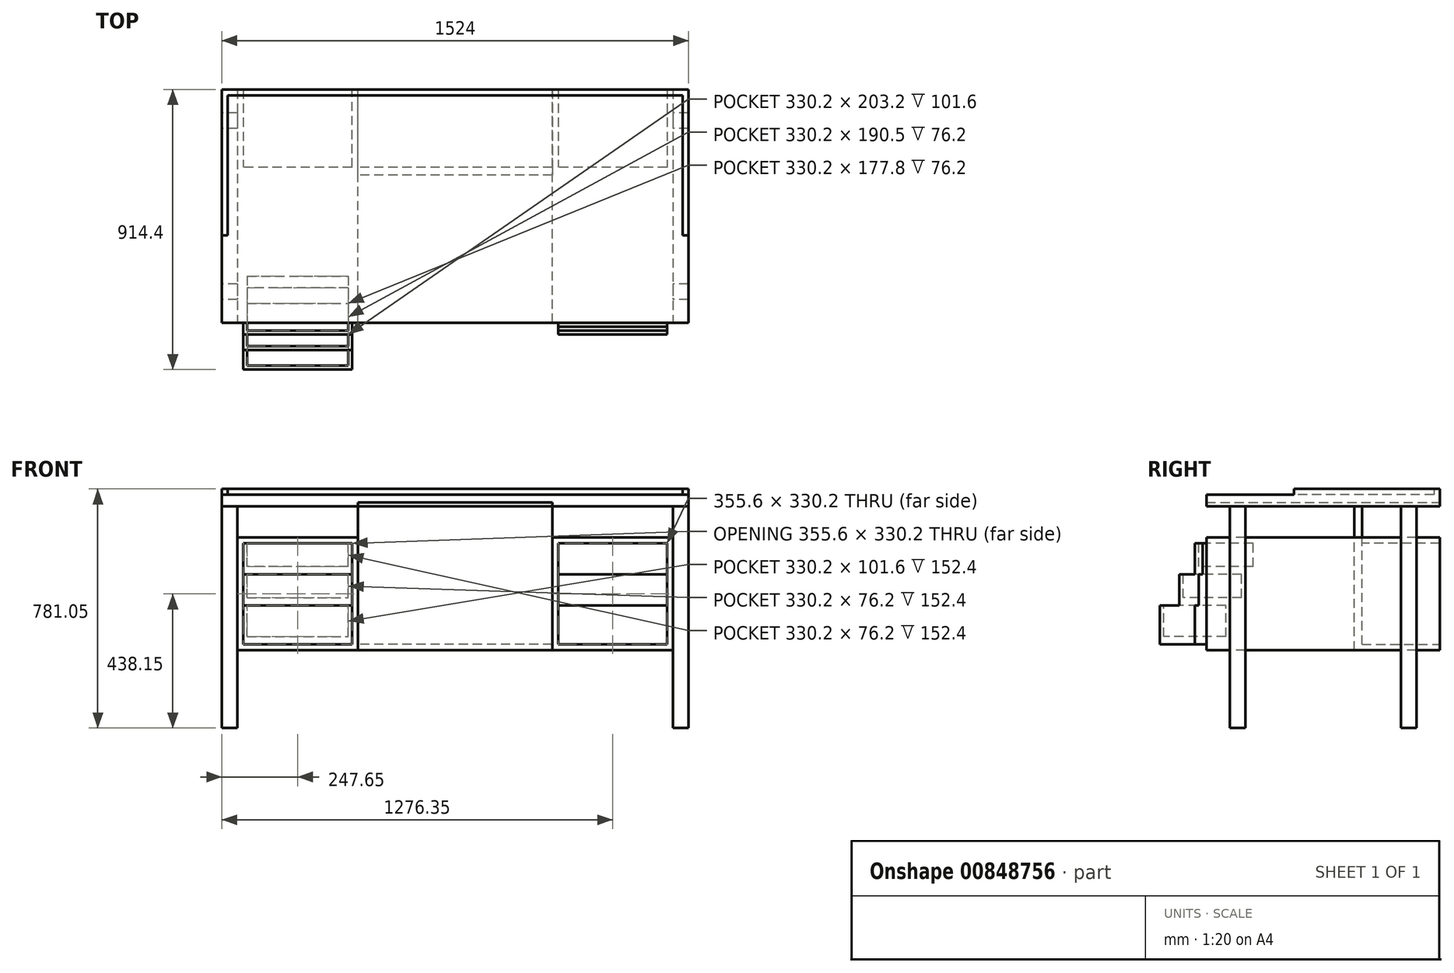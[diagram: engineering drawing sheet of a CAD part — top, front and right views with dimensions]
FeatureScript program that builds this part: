
annotation { "Feature Type Name" : "Feature", "Feature Type Description" : "" }
export const myFeature = defineFeature(function(context is Context, id is Id, definition is map)
    precondition{}
    {
        {
            var Q0;
            Q0=qCreatedBy(makeId("Top.planeOp"),FACE);
            var sketch = newSketch(context, id + "F0", { "sketchPlane" : qUnion([Q0])});
            skLineSegment(sketch, "E0.bottom", {"start": v(-762, -381) * mm, "end": v(762, -381) * mm});
            skLineSegment(sketch, "E0.top", {"start": v(-762, 381) * mm, "end": v(762, 381) * mm});
            skLineSegment(sketch, "E0.left", {"start": v(-762, -381) * mm, "end": v(-762, 381) * mm});
            skLineSegment(sketch, "E0.right", {"start": v(762, -381) * mm, "end": v(762, 381) * mm});
            skPoint(sketch, "E0.middle", {"position": v(0, 0) * mm});
            skSolve(sketch);
        }
        {
            var Q0;
            Q0=makeQuery(id+"F0.imprint","IMPRINT",FACE,{"disambiguationData":[TD([[makeQuery(id+"F0.imprint","IMPRINT",EDGE,{"derivedFrom":sQuery(id+"F0.wireOp",EDGE,"E0.bottom")}),1.0]])]});
            var Q1;
            Q1=sQuery(id+"F0.wireOp",EDGE,"E0.bottom");
            extrude(context, id + "F1", {"entities" : qUnion([Q0]), "surfaceEntities" : qUnion([Q1]), "depth" : 762 * mm, "offsetDistance" : 25.4 * mm});
        }
        {
            var Q0;
            Q0=makeQuery(id+"F1.opExtrude","SWEPT_FACE",FACE,{"disambiguationData":[OSD([sQuery(id+"F0.wireOp",EDGE,"E0.bottom")])]});
            var sketch = newSketch(context, id + "F2", { "sketchPlane" : qUnion([Q0])});
            skLineSegment(sketch, "E1.bottom", {"start": v(-762, 723.9) * mm, "end": v(762, 723.9) * mm});
            skLineSegment(sketch, "E1.top", {"start": v(-762, 622.3) * mm, "end": v(762, 622.3) * mm});
            skLineSegment(sketch, "E1.left", {"start": v(-762, 723.9) * mm, "end": v(-762, 622.3) * mm});
            skLineSegment(sketch, "E1.right", {"start": v(762, 723.9) * mm, "end": v(762, 622.3) * mm});
            skSolve(sketch);
        }
        {
            var Q0;
            Q0=makeQuery(id+"F2.imprint","IMPRINT",FACE,{"disambiguationData":[TD([[makeQuery(id+"F2.imprint","IMPRINT",EDGE,{"derivedFrom":sQuery(id+"F2.wireOp",EDGE,"E1.bottom")}),-1.0]])]});
            var Q1;
            Q1=sQuery(id+"F2.wireOp",EDGE,"E1.right");
            var Q2;
            Q2=sQuery(id+"F2.wireOp",EDGE,"E1.top");
            var Q3;
            Q3=sQuery(id+"F2.wireOp",EDGE,"E1.left");
            var Q4;
            Q4=sQuery(id+"F2.wireOp",EDGE,"E1.bottom");
            extrude(context, id + "F3", {"entities" : qUnion([Q0]), "operationType" : NewBodyOperationType.REMOVE, "surfaceEntities" : qUnion([Q1, Q2, Q3, Q4]), "oppositeDirection" : true, "depth" : 914.4 * mm, "offsetDistance" : 25.4 * mm});
        }
        {
            var Q0;
            Q0=makeQuery(id+"F1.opExtrude","CAP_FACE",FACE,{"disambiguationData":[OSD([sQuery(id+"F0.wireOp",EDGE,"E0.bottom"),sQuery(id+"F0.wireOp",EDGE,"E0.top"),sQuery(id+"F0.wireOp",EDGE,"E0.left"),sQuery(id+"F0.wireOp",EDGE,"E0.right")])],"isStart":true});
            var sketch = newSketch(context, id + "F4", { "sketchPlane" : qUnion([Q0])});
            skLineSegment(sketch, "E2.bottom", {"start": v(0, 0) * mm, "end": v(0, 0) * mm});
            skLineSegment(sketch, "E2.top", {"start": v(0, 0) * mm, "end": v(0, 0) * mm});
            skLineSegment(sketch, "E2.left", {"start": v(0, 0) * mm, "end": v(0, 0) * mm});
            skLineSegment(sketch, "E2.right", {"start": v(0, 0) * mm, "end": v(0, 0) * mm});
            skPoint(sketch, "E2.middle", {"position": v(0, 0) * mm});
            skLineSegment(sketch, "E3.bottom", {"start": v(317.5, 381) * mm, "end": v(-317.5, 381) * mm});
            skLineSegment(sketch, "E3.top", {"start": v(317.5, -381) * mm, "end": v(-317.5, -381) * mm});
            skLineSegment(sketch, "E3.left", {"start": v(317.5, 381) * mm, "end": v(317.5, -381) * mm});
            skLineSegment(sketch, "E3.right", {"start": v(-317.5, 381) * mm, "end": v(-317.5, -381) * mm});
            skSolve(sketch);
        }
        {
            var Q0;
            Q0=qSketchRegion(id+"F4",true);
            extrude(context, id + "F5", {"entities" : qUnion([Q0]), "operationType" : NewBodyOperationType.REMOVE, "oppositeDirection" : true, "depth" : 736.6 * mm, "offsetDistance" : 25.4 * mm});
        }
        {
            var Q0;
            {var subQ0=sQuery(id+"F0.wireOp",EDGE,"E0.bottom");var subQ1=sQuery(id+"F0.wireOp",EDGE,"E0.right");var subQ2=sQuery(id+"F0.wireOp",EDGE,"E0.top");Q0=makeQuery(id+"F5.boolean.opBoolean","SPLIT",FACE,{"disambiguationData":[TD([makeQuery(id+"F1.opExtrude","SWEPT_FACE",FACE,{"disambiguationData":[OSD([subQ1])]})])],"derivedFrom":makeQuery(id+"F1.opExtrude","CAP_FACE",FACE,{"disambiguationData":[OSD([subQ0,subQ2,sQuery(id+"F0.wireOp",EDGE,"E0.left"),subQ1])],"isStart":true})});}
            var sketch = newSketch(context, id + "F6", { "sketchPlane" : qUnion([Q0])});
            skLineSegment(sketch, "E4.bottom", {"start": v(711.2, -381) * mm, "end": v(762, -381) * mm});
            skLineSegment(sketch, "E4.top", {"start": v(711.2, 381) * mm, "end": v(762, 381) * mm});
            skLineSegment(sketch, "E4.left", {"start": v(711.2, -381) * mm, "end": v(711.2, 381) * mm});
            skLineSegment(sketch, "E4.right", {"start": v(762, -381) * mm, "end": v(762, 381) * mm});
            skSolve(sketch);
        }
        {
            var Q0;
            Q0=qSketchRegion(id+"F6",true);
            extrude(context, id + "F7", {"entities" : qUnion([Q0]), "operationType" : NewBodyOperationType.REMOVE, "oppositeDirection" : true, "depth" : 711.2 * mm, "offsetDistance" : 25.4 * mm});
        }
        {
            var Q0;
            {var subQ0=sQuery(id+"F0.wireOp",EDGE,"E0.bottom");var subQ1=sQuery(id+"F0.wireOp",EDGE,"E0.top");var subQ2=sQuery(id+"F0.wireOp",EDGE,"E0.left");Q0=makeQuery(id+"F5.boolean.opBoolean","SPLIT",FACE,{"disambiguationData":[TD([makeQuery(id+"F1.opExtrude","SWEPT_FACE",FACE,{"disambiguationData":[OSD([subQ2])]})])],"derivedFrom":makeQuery(id+"F1.opExtrude","CAP_FACE",FACE,{"disambiguationData":[OSD([subQ0,subQ1,subQ2,sQuery(id+"F0.wireOp",EDGE,"E0.right")])],"isStart":true})});}
            var sketch = newSketch(context, id + "F8", { "sketchPlane" : qUnion([Q0])});
            skLineSegment(sketch, "E5.bottom", {"start": v(-711.2, -381) * mm, "end": v(-762, -381) * mm});
            skLineSegment(sketch, "E5.top", {"start": v(-711.2, 381) * mm, "end": v(-762, 381) * mm});
            skLineSegment(sketch, "E5.left", {"start": v(-711.2, -381) * mm, "end": v(-711.2, 381) * mm});
            skLineSegment(sketch, "E5.right", {"start": v(-762, -381) * mm, "end": v(-762, 381) * mm});
            skSolve(sketch);
        }
        {
            var Q0;
            Q0=qSketchRegion(id+"F8",true);
            extrude(context, id + "F9", {"entities" : qUnion([Q0]), "operationType" : NewBodyOperationType.REMOVE, "oppositeDirection" : true, "depth" : 711.2 * mm, "offsetDistance" : 25.4 * mm});
        }
        {
            var Q0;
            Q0=makeQuery(id+"F3.boolean.opBoolean","COPY",FACE,{"derivedFrom":makeQuery(id+"F3.opExtrude","SWEPT_FACE",FACE,{"disambiguationData":[OSD([sQuery(id+"F2.wireOp",EDGE,"E1.bottom")])]})});
            var sketch = newSketch(context, id + "F10", { "sketchPlane" : qUnion([Q0])});
            skLineSegment(sketch, "E6.bottom", {"start": v(762, 254) * mm, "end": v(711.2, 254) * mm});
            skLineSegment(sketch, "E6.top", {"start": v(762, 304.8) * mm, "end": v(711.2, 304.8) * mm});
            skLineSegment(sketch, "E6.left", {"start": v(762, 254) * mm, "end": v(762, 304.8) * mm});
            skLineSegment(sketch, "E6.right", {"start": v(711.2, 254) * mm, "end": v(711.2, 304.8) * mm});
            skSolve(sketch);
        }
        {
            var Q0;
            Q0=qSketchRegion(id+"F10",true);
            extrude(context, id + "F11", {"entities" : qUnion([Q0]), "depth" : 723.9 * mm, "offsetDistance" : 25.4 * mm});
        }
        {
            var Q0;
            Q0=makeQuery(id+"F3.boolean.opBoolean","COPY",FACE,{"derivedFrom":makeQuery(id+"F3.opExtrude","SWEPT_FACE",FACE,{"disambiguationData":[OSD([sQuery(id+"F2.wireOp",EDGE,"E1.bottom")])]})});
            var sketch = newSketch(context, id + "F12", { "sketchPlane" : qUnion([Q0])});
            skLineSegment(sketch, "E7.bottom", {"start": v(762, -304.8) * mm, "end": v(711.2, -304.8) * mm});
            skLineSegment(sketch, "E7.top", {"start": v(762, -254) * mm, "end": v(711.2, -254) * mm});
            skLineSegment(sketch, "E7.left", {"start": v(762, -304.8) * mm, "end": v(762, -254) * mm});
            skLineSegment(sketch, "E7.right", {"start": v(711.2, -304.8) * mm, "end": v(711.2, -254) * mm});
            skSolve(sketch);
        }
        {
            var Q0;
            Q0=qSketchRegion(id+"F12",true);
            extrude(context, id + "F13", {"entities" : qUnion([Q0]), "depth" : 723.9 * mm, "offsetDistance" : 25.4 * mm});
        }
        {
            var Q0;
            Q0=makeQuery(id+"F3.boolean.opBoolean","COPY",FACE,{"derivedFrom":makeQuery(id+"F3.opExtrude","SWEPT_FACE",FACE,{"disambiguationData":[OSD([sQuery(id+"F2.wireOp",EDGE,"E1.bottom")])]})});
            var sketch = newSketch(context, id + "F14", { "sketchPlane" : qUnion([Q0])});
            skLineSegment(sketch, "E8.bottom", {"start": v(-711.2, 254) * mm, "end": v(-762, 254) * mm});
            skLineSegment(sketch, "E8.top", {"start": v(-711.2, 304.8) * mm, "end": v(-762, 304.8) * mm});
            skLineSegment(sketch, "E8.left", {"start": v(-711.2, 254) * mm, "end": v(-711.2, 304.8) * mm});
            skLineSegment(sketch, "E8.right", {"start": v(-762, 254) * mm, "end": v(-762, 304.8) * mm});
            skSolve(sketch);
        }
        {
            var Q0;
            Q0=qSketchRegion(id+"F14",true);
            extrude(context, id + "F15", {"entities" : qUnion([Q0]), "depth" : 723.9 * mm, "offsetDistance" : 25.4 * mm});
        }
        {
            var Q0;
            Q0=makeQuery(id+"F3.boolean.opBoolean","COPY",FACE,{"derivedFrom":makeQuery(id+"F3.opExtrude","SWEPT_FACE",FACE,{"disambiguationData":[OSD([sQuery(id+"F2.wireOp",EDGE,"E1.bottom")])]})});
            var sketch = newSketch(context, id + "F16", { "sketchPlane" : qUnion([Q0])});
            skLineSegment(sketch, "E9.bottom", {"start": v(-711.2, -304.8) * mm, "end": v(-762, -304.8) * mm});
            skLineSegment(sketch, "E9.top", {"start": v(-711.2, -254) * mm, "end": v(-762, -254) * mm});
            skLineSegment(sketch, "E9.left", {"start": v(-711.2, -304.8) * mm, "end": v(-711.2, -254) * mm});
            skLineSegment(sketch, "E9.right", {"start": v(-762, -304.8) * mm, "end": v(-762, -254) * mm});
            skSolve(sketch);
        }
        {
            var Q0;
            Q0=qSketchRegion(id+"F16",true);
            extrude(context, id + "F17", {"entities" : qUnion([Q0]), "depth" : 723.9 * mm, "offsetDistance" : 25.4 * mm});
        }
        {
            var Q0;
            {var subQ1=sQuery(id+"F0.wireOp",EDGE,"E0.left");var subQ2=sQuery(id+"F0.wireOp",EDGE,"E0.bottom");var subQ4=makeQuery(id+"F1.opExtrude","SWEPT_FACE",FACE,{"disambiguationData":[OSD([subQ1])]});var subQ5=makeQuery(id+"F3.opExtrude","SWEPT_FACE",FACE,{"disambiguationData":[OSD([sQuery(id+"F2.wireOp",EDGE,"E1.top")])]});Q0=makeQuery(id+"F5.boolean.opBoolean","SPLIT",FACE,{"disambiguationData":[TD([subQ4])],"derivedFrom":makeQuery(id+"F3.boolean.opBoolean","SPLIT",FACE,{"disambiguationData":[TD([subQ5])],"derivedFrom":makeQuery(id+"F1.opExtrude","SWEPT_FACE",FACE,{"disambiguationData":[OSD([subQ2])]})})});}
            var sketch = newSketch(context, id + "F18", { "sketchPlane" : qUnion([Q0])});
            skLineSegment(sketch, "E10.bottom", {"start": v(-711.2, 254) * mm, "end": v(-317.5, 254) * mm});
            skLineSegment(sketch, "E10.top", {"start": v(-711.2, 0) * mm, "end": v(-317.5, 0) * mm});
            skLineSegment(sketch, "E10.left", {"start": v(-711.2, 254) * mm, "end": v(-711.2, 0) * mm});
            skLineSegment(sketch, "E10.right", {"start": v(-317.5, 254) * mm, "end": v(-317.5, 0) * mm});
            skSolve(sketch);
        }
        {
            var Q0;
            Q0=qSketchRegion(id+"F18",true);
            extrude(context, id + "F19", {"entities" : qUnion([Q0]), "operationType" : NewBodyOperationType.REMOVE, "oppositeDirection" : true, "depth" : 762 * mm, "offsetDistance" : 25.4 * mm});
        }
        {
            var Q0;
            {var subQ0=sQuery(id+"F0.wireOp",EDGE,"E0.right");var subQ2=sQuery(id+"F0.wireOp",EDGE,"E0.bottom");var subQ4=makeQuery(id+"F1.opExtrude","SWEPT_FACE",FACE,{"disambiguationData":[OSD([subQ0])]});var subQ5=makeQuery(id+"F3.opExtrude","SWEPT_FACE",FACE,{"disambiguationData":[OSD([sQuery(id+"F2.wireOp",EDGE,"E1.top")])]});Q0=makeQuery(id+"F5.boolean.opBoolean","SPLIT",FACE,{"disambiguationData":[TD([subQ4])],"derivedFrom":makeQuery(id+"F3.boolean.opBoolean","SPLIT",FACE,{"disambiguationData":[TD([subQ5])],"derivedFrom":makeQuery(id+"F1.opExtrude","SWEPT_FACE",FACE,{"disambiguationData":[OSD([subQ2])]})})});}
            var sketch = newSketch(context, id + "F20", { "sketchPlane" : qUnion([Q0])});
            skLineSegment(sketch, "E11.bottom", {"start": v(317.5, 0) * mm, "end": v(711.2, 0) * mm});
            skLineSegment(sketch, "E11.top", {"start": v(317.5, 254) * mm, "end": v(711.2, 254) * mm});
            skLineSegment(sketch, "E11.left", {"start": v(317.5, 0) * mm, "end": v(317.5, 254) * mm});
            skLineSegment(sketch, "E11.right", {"start": v(711.2, 0) * mm, "end": v(711.2, 254) * mm});
            skSolve(sketch);
        }
        {
            var Q0;
            Q0=qSketchRegion(id+"F20",true);
            extrude(context, id + "F21", {"entities" : qUnion([Q0]), "operationType" : NewBodyOperationType.REMOVE, "oppositeDirection" : true, "depth" : 762 * mm, "offsetDistance" : 25.4 * mm});
        }
        {
            var Q0;
            {var subQ0=sQuery(id+"F0.wireOp",EDGE,"E0.right");var subQ2=sQuery(id+"F0.wireOp",EDGE,"E0.top");var subQ4=makeQuery(id+"F1.opExtrude","SWEPT_FACE",FACE,{"disambiguationData":[OSD([subQ0])]});var subQ5=makeQuery(id+"F3.opExtrude","SWEPT_FACE",FACE,{"disambiguationData":[OSD([sQuery(id+"F2.wireOp",EDGE,"E1.top")])]});Q0=makeQuery(id+"F5.boolean.opBoolean","SPLIT",FACE,{"disambiguationData":[TD([subQ4])],"derivedFrom":makeQuery(id+"F3.boolean.opBoolean","SPLIT",FACE,{"disambiguationData":[TD([subQ5])],"derivedFrom":makeQuery(id+"F1.opExtrude","SWEPT_FACE",FACE,{"disambiguationData":[OSD([subQ2])]})})});}
            var sketch = newSketch(context, id + "F22", { "sketchPlane" : qUnion([Q0])});
            skLineSegment(sketch, "E12.bottom", {"start": v(-692.15, 273.05) * mm, "end": v(-336.55, 273.05) * mm});
            skLineSegment(sketch, "E12.top", {"start": v(-692.15, 628.65) * mm, "end": v(-336.55, 628.65) * mm});
            skLineSegment(sketch, "E12.left", {"start": v(-692.15, 273.05) * mm, "end": v(-692.15, 628.65) * mm});
            skLineSegment(sketch, "E12.right", {"start": v(-336.55, 273.05) * mm, "end": v(-336.55, 628.65) * mm});
            skSolve(sketch);
        }
        {
            var Q0;
            Q0=qSketchRegion(id+"F22",true);
            extrude(context, id + "F23", {"entities" : qUnion([Q0]), "operationType" : NewBodyOperationType.REMOVE, "oppositeDirection" : true, "depth" : 254 * mm, "offsetDistance" : 25.4 * mm});
        }
        {
            var Q0;
            {var subQ1=sQuery(id+"F0.wireOp",EDGE,"E0.left");var subQ2=sQuery(id+"F0.wireOp",EDGE,"E0.top");var subQ4=makeQuery(id+"F1.opExtrude","SWEPT_FACE",FACE,{"disambiguationData":[OSD([subQ1])]});var subQ5=makeQuery(id+"F3.opExtrude","SWEPT_FACE",FACE,{"disambiguationData":[OSD([sQuery(id+"F2.wireOp",EDGE,"E1.top")])]});Q0=makeQuery(id+"F5.boolean.opBoolean","SPLIT",FACE,{"disambiguationData":[TD([subQ4])],"derivedFrom":makeQuery(id+"F3.boolean.opBoolean","SPLIT",FACE,{"disambiguationData":[TD([subQ5])],"derivedFrom":makeQuery(id+"F1.opExtrude","SWEPT_FACE",FACE,{"disambiguationData":[OSD([subQ2])]})})});}
            var sketch = newSketch(context, id + "F24", { "sketchPlane" : qUnion([Q0])});
            skLineSegment(sketch, "E13.bottom", {"start": v(336.55, 603.25) * mm, "end": v(692.15, 603.25) * mm});
            skLineSegment(sketch, "E13.top", {"start": v(336.55, 247.65) * mm, "end": v(692.15, 247.65) * mm});
            skLineSegment(sketch, "E13.left", {"start": v(336.55, 603.25) * mm, "end": v(336.55, 247.65) * mm});
            skLineSegment(sketch, "E13.right", {"start": v(692.15, 603.25) * mm, "end": v(692.15, 247.65) * mm});
            skSolve(sketch);
        }
        {
            var Q0;
            Q0=qSketchRegion(id+"F24",true);
            extrude(context, id + "F25", {"entities" : qUnion([Q0]), "operationType" : NewBodyOperationType.REMOVE, "oppositeDirection" : true, "depth" : 254 * mm, "offsetDistance" : 25.4 * mm});
        }
        {
            var Q0;
            Q0=makeQuery(id+"F3.boolean.opBoolean","COPY",FACE,{"derivedFrom":makeQuery(id+"F3.opExtrude","SWEPT_FACE",FACE,{"disambiguationData":[OSD([sQuery(id+"F2.wireOp",EDGE,"E1.bottom")])]})});
            var sketch = newSketch(context, id + "F26", { "sketchPlane" : qUnion([Q0])});
            skLineSegment(sketch, "E14.bottom", {"start": v(317.5, -381) * mm, "end": v(-317.5, -381) * mm});
            skLineSegment(sketch, "E14.top", {"start": v(317.5, -101.6) * mm, "end": v(-317.5, -101.6) * mm});
            skLineSegment(sketch, "E14.left", {"start": v(317.5, -381) * mm, "end": v(317.5, -101.6) * mm});
            skLineSegment(sketch, "E14.right", {"start": v(-317.5, -381) * mm, "end": v(-317.5, -101.6) * mm});
            skSolve(sketch);
        }
        {
            var Q0;
            Q0=qSketchRegion(id+"F26",true);
            extrude(context, id + "F27", {"entities" : qUnion([Q0]), "depth" : 469.9 * mm, "offsetDistance" : 25.4 * mm});
        }
        {
            var Q0;
            Q0=makeQuery(id+"F27.opExtrude","SWEPT_FACE",FACE,{"disambiguationData":[OSD([sQuery(id+"F26.wireOp",EDGE,"E14.bottom")])]});
            var sketch = newSketch(context, id + "F28", { "sketchPlane" : qUnion([Q0])});
            skLineSegment(sketch, "E15.bottom", {"start": v(-317.5, 723.9) * mm, "end": v(317.5, 723.9) * mm});
            skLineSegment(sketch, "E15.top", {"start": v(-317.5, 273.05) * mm, "end": v(317.5, 273.05) * mm});
            skLineSegment(sketch, "E15.left", {"start": v(-317.5, 723.9) * mm, "end": v(-317.5, 273.05) * mm});
            skLineSegment(sketch, "E15.right", {"start": v(317.5, 723.9) * mm, "end": v(317.5, 273.05) * mm});
            skSolve(sketch);
        }
        {
            var Q0;
            Q0=qSketchRegion(id+"F28",true);
            extrude(context, id + "F29", {"entities" : qUnion([Q0]), "operationType" : NewBodyOperationType.REMOVE, "oppositeDirection" : true, "depth" : 254 * mm, "offsetDistance" : 25.4 * mm});
        }
        {
            var Q0;
            Q0=makeQuery(id+"F23.boolean.opBoolean","COPY",FACE,{"derivedFrom":makeQuery(id+"F23.opExtrude","CAP_FACE",FACE,{"disambiguationData":[OSD([sQuery(id+"F22.wireOp",EDGE,"E12.bottom"),sQuery(id+"F22.wireOp",EDGE,"E12.top"),sQuery(id+"F22.wireOp",EDGE,"E12.left"),sQuery(id+"F22.wireOp",EDGE,"E12.right")])],"isStart":false})});
            var sketch = newSketch(context, id + "F30", { "sketchPlane" : qUnion([Q0])});
            skLineSegment(sketch, "E16.bottom", {"start": v(-692.15, 622.3) * mm, "end": v(-336.55, 622.3) * mm});
            skLineSegment(sketch, "E16.top", {"start": v(-692.15, 603.25) * mm, "end": v(-336.55, 603.25) * mm});
            skLineSegment(sketch, "E16.left", {"start": v(-692.15, 622.3) * mm, "end": v(-692.15, 603.25) * mm});
            skLineSegment(sketch, "E16.right", {"start": v(-336.55, 622.3) * mm, "end": v(-336.55, 603.25) * mm});
            skSolve(sketch);
        }
        {
            var Q0;
            Q0=qSketchRegion(id+"F30",true);
            extrude(context, id + "F31", {"entities" : qUnion([Q0]), "operationType" : NewBodyOperationType.ADD, "depth" : 254 * mm, "offsetDistance" : 25.4 * mm});
        }
        {
            var Q0;
            Q0=makeQuery(id+"F25.boolean.opBoolean","COPY",FACE,{"derivedFrom":makeQuery(id+"F25.opExtrude","CAP_FACE",FACE,{"disambiguationData":[OSD([sQuery(id+"F24.wireOp",EDGE,"E13.bottom"),sQuery(id+"F24.wireOp",EDGE,"E13.top"),sQuery(id+"F24.wireOp",EDGE,"E13.left"),sQuery(id+"F24.wireOp",EDGE,"E13.right")])],"isStart":false})});
            var sketch = newSketch(context, id + "F32", { "sketchPlane" : qUnion([Q0])});
            skLineSegment(sketch, "E17.bottom", {"start": v(336.55, 254) * mm, "end": v(692.15, 254) * mm});
            skLineSegment(sketch, "E17.top", {"start": v(336.55, 273.05) * mm, "end": v(692.15, 273.05) * mm});
            skLineSegment(sketch, "E17.left", {"start": v(336.55, 254) * mm, "end": v(336.55, 273.05) * mm});
            skLineSegment(sketch, "E17.right", {"start": v(692.15, 254) * mm, "end": v(692.15, 273.05) * mm});
            skSolve(sketch);
        }
        {
            var Q0;
            Q0=qSketchRegion(id+"F32",true);
            extrude(context, id + "F33", {"entities" : qUnion([Q0]), "operationType" : NewBodyOperationType.ADD, "depth" : 254 * mm, "offsetDistance" : 25.4 * mm});
        }
        {
            var Q0;
            Q0=makeQuery(id+"F1.opExtrude","CAP_FACE",FACE,{"disambiguationData":[OSD([sQuery(id+"F0.wireOp",EDGE,"E0.bottom"),sQuery(id+"F0.wireOp",EDGE,"E0.top"),sQuery(id+"F0.wireOp",EDGE,"E0.left"),sQuery(id+"F0.wireOp",EDGE,"E0.right")])],"isStart":false});
            var sketch = newSketch(context, id + "F34", { "sketchPlane" : qUnion([Q0])});
            skLineSegment(sketch, "E18.bottom", {"start": v(-762, 381) * mm, "end": v(762, 381) * mm});
            skLineSegment(sketch, "E18.top", {"start": v(-762, 361.95) * mm, "end": v(762, 361.95) * mm});
            skLineSegment(sketch, "E18.left", {"start": v(-762, 381) * mm, "end": v(-762, 361.95) * mm});
            skLineSegment(sketch, "E18.right", {"start": v(762, 381) * mm, "end": v(762, 361.95) * mm});
            skSolve(sketch);
        }
        {
            var Q0;
            Q0=qSketchRegion(id+"F34",true);
            extrude(context, id + "F35", {"entities" : qUnion([Q0]), "operationType" : NewBodyOperationType.ADD, "depth" : 19.05 * mm, "offsetDistance" : 25.4 * mm});
        }
        {
            var Q0;
            Q0=makeQuery(id+"F1.opExtrude","CAP_FACE",FACE,{"disambiguationData":[OSD([sQuery(id+"F0.wireOp",EDGE,"E0.bottom"),sQuery(id+"F0.wireOp",EDGE,"E0.top"),sQuery(id+"F0.wireOp",EDGE,"E0.left"),sQuery(id+"F0.wireOp",EDGE,"E0.right")])],"isStart":false});
            var sketch = newSketch(context, id + "F36", { "sketchPlane" : qUnion([Q0])});
            skLineSegment(sketch, "E19.bottom", {"start": v(-742.95, -95.25) * mm, "end": v(-762, -95.25) * mm});
            skLineSegment(sketch, "E19.top", {"start": v(-742.95, 361.95) * mm, "end": v(-762, 361.95) * mm});
            skLineSegment(sketch, "E19.left", {"start": v(-742.95, -95.25) * mm, "end": v(-742.95, 361.95) * mm});
            skLineSegment(sketch, "E19.right", {"start": v(-762, -95.25) * mm, "end": v(-762, 361.95) * mm});
            skSolve(sketch);
        }
        {
            var Q0;
            Q0=qSketchRegion(id+"F36",true);
            extrude(context, id + "F37", {"entities" : qUnion([Q0]), "operationType" : NewBodyOperationType.ADD, "depth" : 19.05 * mm, "offsetDistance" : 25.4 * mm});
        }
        {
            var Q0;
            Q0=makeQuery(id+"F1.opExtrude","CAP_FACE",FACE,{"disambiguationData":[OSD([sQuery(id+"F0.wireOp",EDGE,"E0.bottom"),sQuery(id+"F0.wireOp",EDGE,"E0.top"),sQuery(id+"F0.wireOp",EDGE,"E0.left"),sQuery(id+"F0.wireOp",EDGE,"E0.right")])],"isStart":false});
            var sketch = newSketch(context, id + "F38", { "sketchPlane" : qUnion([Q0])});
            skLineSegment(sketch, "E20.bottom", {"start": v(762, 361.95) * mm, "end": v(742.95, 361.95) * mm});
            skLineSegment(sketch, "E20.top", {"start": v(762, -95.25) * mm, "end": v(742.95, -95.25) * mm});
            skLineSegment(sketch, "E20.left", {"start": v(762, 361.95) * mm, "end": v(762, -95.25) * mm});
            skLineSegment(sketch, "E20.right", {"start": v(742.95, 361.95) * mm, "end": v(742.95, -95.25) * mm});
            skSolve(sketch);
        }
        {
            var Q0;
            Q0=qSketchRegion(id+"F38",true);
            extrude(context, id + "F39", {"entities" : qUnion([Q0]), "operationType" : NewBodyOperationType.ADD, "depth" : 19.05 * mm, "offsetDistance" : 25.4 * mm});
        }
        {
            var Q0;
            {var subQ1=sQuery(id+"F0.wireOp",EDGE,"E0.left");var subQ2=sQuery(id+"F0.wireOp",EDGE,"E0.bottom");var subQ4=makeQuery(id+"F1.opExtrude","SWEPT_FACE",FACE,{"disambiguationData":[OSD([subQ1])]});var subQ5=makeQuery(id+"F3.opExtrude","SWEPT_FACE",FACE,{"disambiguationData":[OSD([sQuery(id+"F2.wireOp",EDGE,"E1.top")])]});Q0=makeQuery(id+"F5.boolean.opBoolean","SPLIT",FACE,{"disambiguationData":[TD([subQ4])],"derivedFrom":makeQuery(id+"F3.boolean.opBoolean","SPLIT",FACE,{"disambiguationData":[TD([subQ5])],"derivedFrom":makeQuery(id+"F1.opExtrude","SWEPT_FACE",FACE,{"disambiguationData":[OSD([subQ2])]})})});}
            var sketch = newSketch(context, id + "F40", { "sketchPlane" : qUnion([Q0])});
            skLineSegment(sketch, "E21.bottom", {"start": v(-692.15, 603.25) * mm, "end": v(-336.55, 603.25) * mm});
            skLineSegment(sketch, "E21.top", {"start": v(-692.15, 273.05) * mm, "end": v(-336.55, 273.05) * mm});
            skLineSegment(sketch, "E21.left", {"start": v(-692.15, 603.25) * mm, "end": v(-692.15, 273.05) * mm});
            skLineSegment(sketch, "E21.right", {"start": v(-336.55, 603.25) * mm, "end": v(-336.55, 273.05) * mm});
            skSolve(sketch);
        }
        {
            var Q0;
            Q0=qSketchRegion(id+"F40",true);
            extrude(context, id + "F41", {"entities" : qUnion([Q0]), "operationType" : NewBodyOperationType.ADD, "depth" : 152.4 * mm, "offsetDistance" : 25.4 * mm});
        }
        {
            var Q0;
            Q0=makeQuery(id+"F41.opExtrude","CAP_FACE",FACE,{"disambiguationData":[OSD([sQuery(id+"F40.wireOp",EDGE,"E21.bottom"),sQuery(id+"F40.wireOp",EDGE,"E21.top"),sQuery(id+"F40.wireOp",EDGE,"E21.left"),sQuery(id+"F40.wireOp",EDGE,"E21.right")])],"isStart":false});
            var sketch = newSketch(context, id + "F42", { "sketchPlane" : qUnion([Q0])});
            skLineSegment(sketch, "E22.bottom", {"start": v(-336.55, 603.25) * mm, "end": v(-692.15, 603.25) * mm});
            skLineSegment(sketch, "E22.top", {"start": v(-336.55, 501.65) * mm, "end": v(-692.15, 501.65) * mm});
            skLineSegment(sketch, "E22.left", {"start": v(-336.55, 603.25) * mm, "end": v(-336.55, 501.65) * mm});
            skLineSegment(sketch, "E22.right", {"start": v(-692.15, 603.25) * mm, "end": v(-692.15, 501.65) * mm});
            skSolve(sketch);
        }
        {
            var Q0;
            Q0=makeQuery(id+"F42.imprint","IMPRINT",FACE,{"disambiguationData":[TD([[makeQuery(id+"F42.imprint","IMPRINT",EDGE,{"derivedFrom":sQuery(id+"F42.wireOp",EDGE,"E22.bottom")}),-1.0]])]});
            var Q1;
            Q1=sQuery(id+"F42.wireOp",EDGE,"E22.left");
            extrude(context, id + "F43", {"entities" : qUnion([Q0]), "operationType" : NewBodyOperationType.REMOVE, "surfaceOperationType" : NewSurfaceOperationType.ADD, "surfaceEntities" : qUnion([Q1]), "oppositeDirection" : true, "depth" : 114.3 * mm, "offsetDistance" : 25.4 * mm});
        }
        {
            var Q0;
            Q0=makeQuery(id+"F41.opExtrude","CAP_FACE",FACE,{"disambiguationData":[OSD([sQuery(id+"F40.wireOp",EDGE,"E21.bottom"),sQuery(id+"F40.wireOp",EDGE,"E21.top"),sQuery(id+"F40.wireOp",EDGE,"E21.left"),sQuery(id+"F40.wireOp",EDGE,"E21.right")])],"isStart":false});
            var sketch = newSketch(context, id + "F44", { "sketchPlane" : qUnion([Q0])});
            skLineSegment(sketch, "E23.bottom", {"start": v(-692.15, 501.65) * mm, "end": v(-336.55, 501.65) * mm});
            skLineSegment(sketch, "E23.top", {"start": v(-692.15, 400.05) * mm, "end": v(-336.55, 400.05) * mm});
            skLineSegment(sketch, "E23.left", {"start": v(-692.15, 501.65) * mm, "end": v(-692.15, 400.05) * mm});
            skLineSegment(sketch, "E23.right", {"start": v(-336.55, 501.65) * mm, "end": v(-336.55, 400.05) * mm});
            skSolve(sketch);
        }
        {
            var Q0;
            Q0=qSketchRegion(id+"F44",true);
            extrude(context, id + "F45", {"entities" : qUnion([Q0]), "operationType" : NewBodyOperationType.REMOVE, "oppositeDirection" : true, "depth" : 63.5 * mm, "offsetDistance" : 25.4 * mm});
        }
        {
            var Q0;
            Q0=makeQuery(id+"F45.boolean.opBoolean","COPY",FACE,{"derivedFrom":makeQuery(id+"F45.opExtrude","SWEPT_FACE",FACE,{"disambiguationData":[OSD([sQuery(id+"F44.wireOp",EDGE,"E23.top")])]})});
            var sketch = newSketch(context, id + "F46", { "sketchPlane" : qUnion([Q0])});
            skLineSegment(sketch, "E24.bottom", {"start": v(-679.45, -469.9) * mm, "end": v(-349.25, -469.9) * mm});
            skLineSegment(sketch, "E24.top", {"start": v(-679.45, -520.7) * mm, "end": v(-349.25, -520.7) * mm});
            skLineSegment(sketch, "E24.left", {"start": v(-679.45, -469.9) * mm, "end": v(-679.45, -520.7) * mm});
            skLineSegment(sketch, "E24.right", {"start": v(-349.25, -469.9) * mm, "end": v(-349.25, -520.7) * mm});
            skSolve(sketch);
        }
        {
            var Q0;
            Q0=qSketchRegion(id+"F46",true);
            extrude(context, id + "F47", {"entities" : qUnion([Q0]), "operationType" : NewBodyOperationType.REMOVE, "oppositeDirection" : true, "depth" : 101.6 * mm, "offsetDistance" : 25.4 * mm});
        }
        {
            var Q0;
            Q0=makeQuery(id+"F47.boolean.opBoolean","MERGE",FACE,{"derivedFrom":[makeQuery(id+"F45.boolean.opBoolean","COPY",FACE,{"derivedFrom":makeQuery(id+"F45.opExtrude","CAP_FACE",FACE,{"disambiguationData":[OSD([sQuery(id+"F44.wireOp",EDGE,"E23.bottom"),sQuery(id+"F44.wireOp",EDGE,"E23.top"),sQuery(id+"F44.wireOp",EDGE,"E23.left"),sQuery(id+"F44.wireOp",EDGE,"E23.right")])],"isStart":false})}),makeQuery(id+"F47.opExtrude","SWEPT_FACE",FACE,{"disambiguationData":[OSD([sQuery(id+"F46.wireOp",EDGE,"E24.bottom")])]})]});
            var sketch = newSketch(context, id + "F48", { "sketchPlane" : qUnion([Q0])});
            skLineSegment(sketch, "E25.bottom", {"start": v(-349.25, 400.05) * mm, "end": v(-679.45, 400.05) * mm});
            skLineSegment(sketch, "E25.top", {"start": v(-349.25, 298.45) * mm, "end": v(-679.45, 298.45) * mm});
            skLineSegment(sketch, "E25.left", {"start": v(-349.25, 400.05) * mm, "end": v(-349.25, 298.45) * mm});
            skLineSegment(sketch, "E25.right", {"start": v(-679.45, 400.05) * mm, "end": v(-679.45, 298.45) * mm});
            skSolve(sketch);
        }
        {
            var Q0;
            Q0=qSketchRegion(id+"F48",true);
            extrude(context, id + "F49", {"entities" : qUnion([Q0]), "operationType" : NewBodyOperationType.REMOVE, "oppositeDirection" : true, "depth" : 152.4 * mm, "offsetDistance" : 25.4 * mm});
        }
        {
            var Q0;
            Q0=makeQuery(id+"F43.boolean.opBoolean","COPY",FACE,{"derivedFrom":makeQuery(id+"F43.opExtrude","SWEPT_FACE",FACE,{"disambiguationData":[OSD([sQuery(id+"F42.wireOp",EDGE,"E22.top")])]})});
            var sketch = newSketch(context, id + "F50", { "sketchPlane" : qUnion([Q0])});
            skLineSegment(sketch, "E26.bottom", {"start": v(-679.45, -419.1) * mm, "end": v(-349.25, -419.1) * mm});
            skLineSegment(sketch, "E26.top", {"start": v(-679.45, -457.2) * mm, "end": v(-349.25, -457.2) * mm});
            skLineSegment(sketch, "E26.left", {"start": v(-679.45, -419.1) * mm, "end": v(-679.45, -457.2) * mm});
            skLineSegment(sketch, "E26.right", {"start": v(-349.25, -419.1) * mm, "end": v(-349.25, -457.2) * mm});
            skSolve(sketch);
        }
        {
            var Q0;
            Q0=qSketchRegion(id+"F50",true);
            extrude(context, id + "F51", {"entities" : qUnion([Q0]), "operationType" : NewBodyOperationType.REMOVE, "oppositeDirection" : true, "depth" : 76.2 * mm, "offsetDistance" : 25.4 * mm});
        }
        {
            var Q0;
            Q0=makeQuery(id+"F51.boolean.opBoolean","MERGE",FACE,{"derivedFrom":[makeQuery(id+"F43.boolean.opBoolean","COPY",FACE,{"derivedFrom":makeQuery(id+"F43.opExtrude","CAP_FACE",FACE,{"disambiguationData":[OSD([sQuery(id+"F42.wireOp",EDGE,"E22.bottom"),sQuery(id+"F42.wireOp",EDGE,"E22.top"),sQuery(id+"F42.wireOp",EDGE,"E22.left"),sQuery(id+"F42.wireOp",EDGE,"E22.right")])],"isStart":false})}),makeQuery(id+"F51.opExtrude","SWEPT_FACE",FACE,{"disambiguationData":[OSD([sQuery(id+"F50.wireOp",EDGE,"E26.bottom")])]})]});
            var sketch = newSketch(context, id + "F52", { "sketchPlane" : qUnion([Q0])});
            skLineSegment(sketch, "E27.bottom", {"start": v(-349.25, 425.45) * mm, "end": v(-679.45, 425.45) * mm});
            skLineSegment(sketch, "E27.top", {"start": v(-349.25, 501.65) * mm, "end": v(-679.45, 501.65) * mm});
            skLineSegment(sketch, "E27.left", {"start": v(-349.25, 425.45) * mm, "end": v(-349.25, 501.65) * mm});
            skLineSegment(sketch, "E27.right", {"start": v(-679.45, 425.45) * mm, "end": v(-679.45, 501.65) * mm});
            skSolve(sketch);
        }
        {
            var Q0;
            Q0=qSketchRegion(id+"F52",true);
            extrude(context, id + "F53", {"entities" : qUnion([Q0]), "operationType" : NewBodyOperationType.REMOVE, "oppositeDirection" : true, "depth" : 152.4 * mm, "offsetDistance" : 25.4 * mm});
        }
        {
            var Q0;
            Q0=makeQuery(id+"F41.opExtrude","SWEPT_FACE",FACE,{"disambiguationData":[OSD([sQuery(id+"F40.wireOp",EDGE,"E21.bottom")])]});
            var sketch = newSketch(context, id + "F54", { "sketchPlane" : qUnion([Q0])});
            skLineSegment(sketch, "E28.bottom", {"start": v(-349.25, -381) * mm, "end": v(-679.45, -381) * mm});
            skLineSegment(sketch, "E28.top", {"start": v(-349.25, -406.4) * mm, "end": v(-679.45, -406.4) * mm});
            skLineSegment(sketch, "E28.left", {"start": v(-349.25, -381) * mm, "end": v(-349.25, -406.4) * mm});
            skLineSegment(sketch, "E28.right", {"start": v(-679.45, -381) * mm, "end": v(-679.45, -406.4) * mm});
            skSolve(sketch);
        }
        {
            var Q0;
            Q0=qSketchRegion(id+"F54",true);
            extrude(context, id + "F55", {"entities" : qUnion([Q0]), "operationType" : NewBodyOperationType.REMOVE, "oppositeDirection" : true, "depth" : 76.2 * mm, "offsetDistance" : 25.4 * mm});
        }
        {
            var Q0;
            {var subQ1=sQuery(id+"F0.wireOp",EDGE,"E0.left");var subQ2=sQuery(id+"F0.wireOp",EDGE,"E0.bottom");var subQ4=makeQuery(id+"F1.opExtrude","SWEPT_FACE",FACE,{"disambiguationData":[OSD([subQ1])]});var subQ5=makeQuery(id+"F3.opExtrude","SWEPT_FACE",FACE,{"disambiguationData":[OSD([sQuery(id+"F2.wireOp",EDGE,"E1.top")])]});Q0=makeQuery(id+"F55.boolean.opBoolean","MERGE",FACE,{"derivedFrom":[makeQuery(id+"F5.boolean.opBoolean","SPLIT",FACE,{"disambiguationData":[TD([subQ4])],"derivedFrom":makeQuery(id+"F3.boolean.opBoolean","SPLIT",FACE,{"disambiguationData":[TD([subQ5])],"derivedFrom":makeQuery(id+"F1.opExtrude","SWEPT_FACE",FACE,{"disambiguationData":[OSD([subQ2])]})})}),makeQuery(id+"F55.opExtrude","SWEPT_FACE",FACE,{"disambiguationData":[OSD([sQuery(id+"F54.wireOp",EDGE,"E28.bottom")])]})]});}
            var sketch = newSketch(context, id + "F56", { "sketchPlane" : qUnion([Q0])});
            skLineSegment(sketch, "E29.bottom", {"start": v(-349.25, 527.05) * mm, "end": v(-679.45, 527.05) * mm});
            skLineSegment(sketch, "E29.top", {"start": v(-349.25, 603.25) * mm, "end": v(-679.45, 603.25) * mm});
            skLineSegment(sketch, "E29.left", {"start": v(-349.25, 527.05) * mm, "end": v(-349.25, 603.25) * mm});
            skLineSegment(sketch, "E29.right", {"start": v(-679.45, 527.05) * mm, "end": v(-679.45, 603.25) * mm});
            skSolve(sketch);
        }
        {
            var Q0;
            Q0=qSketchRegion(id+"F56",true);
            extrude(context, id + "F57", {"entities" : qUnion([Q0]), "operationType" : NewBodyOperationType.REMOVE, "oppositeDirection" : true, "depth" : 152.4 * mm, "offsetDistance" : 25.4 * mm});
        }
        {
            var Q0;
            {var subQ0=sQuery(id+"F0.wireOp",EDGE,"E0.right");var subQ2=sQuery(id+"F0.wireOp",EDGE,"E0.bottom");var subQ4=makeQuery(id+"F1.opExtrude","SWEPT_FACE",FACE,{"disambiguationData":[OSD([subQ0])]});var subQ5=makeQuery(id+"F3.opExtrude","SWEPT_FACE",FACE,{"disambiguationData":[OSD([sQuery(id+"F2.wireOp",EDGE,"E1.top")])]});Q0=makeQuery(id+"F5.boolean.opBoolean","SPLIT",FACE,{"disambiguationData":[TD([subQ4])],"derivedFrom":makeQuery(id+"F3.boolean.opBoolean","SPLIT",FACE,{"disambiguationData":[TD([subQ5])],"derivedFrom":makeQuery(id+"F1.opExtrude","SWEPT_FACE",FACE,{"disambiguationData":[OSD([subQ2])]})})});}
            var sketch = newSketch(context, id + "F58", { "sketchPlane" : qUnion([Q0])});
            skLineSegment(sketch, "E30.bottom", {"start": v(336.55, 603.25) * mm, "end": v(692.15, 603.25) * mm});
            skLineSegment(sketch, "E30.top", {"start": v(336.55, 273.05) * mm, "end": v(692.15, 273.05) * mm});
            skLineSegment(sketch, "E30.left", {"start": v(336.55, 603.25) * mm, "end": v(336.55, 273.05) * mm});
            skLineSegment(sketch, "E30.right", {"start": v(692.15, 603.25) * mm, "end": v(692.15, 273.05) * mm});
            skSolve(sketch);
        }
        {
            var Q0;
            Q0=qSketchRegion(id+"F58",true);
            extrude(context, id + "F59", {"entities" : qUnion([Q0]), "operationType" : NewBodyOperationType.ADD, "depth" : 38.1 * mm, "offsetDistance" : 25.4 * mm});
        }
        {
            var Q0;
            Q0=makeQuery(id+"F59.opExtrude","CAP_FACE",FACE,{"disambiguationData":[OSD([sQuery(id+"F58.wireOp",EDGE,"E30.bottom"),sQuery(id+"F58.wireOp",EDGE,"E30.top"),sQuery(id+"F58.wireOp",EDGE,"E30.left"),sQuery(id+"F58.wireOp",EDGE,"E30.right")])],"isStart":false});
            var sketch = newSketch(context, id + "F60", { "sketchPlane" : qUnion([Q0])});
            skLineSegment(sketch, "E31.bottom", {"start": v(336.55, 603.25) * mm, "end": v(692.15, 603.25) * mm});
            skLineSegment(sketch, "E31.top", {"start": v(336.55, 501.65) * mm, "end": v(692.15, 501.65) * mm});
            skLineSegment(sketch, "E31.left", {"start": v(336.55, 603.25) * mm, "end": v(336.55, 501.65) * mm});
            skLineSegment(sketch, "E31.right", {"start": v(692.15, 603.25) * mm, "end": v(692.15, 501.65) * mm});
            skSolve(sketch);
        }
        {
            var Q0;
            Q0=qSketchRegion(id+"F60",true);
            extrude(context, id + "F61", {"entities" : qUnion([Q0]), "operationType" : NewBodyOperationType.REMOVE, "oppositeDirection" : true, "depth" : 25.4 * mm, "offsetDistance" : 25.4 * mm});
        }
        {
            var Q0;
            Q0=makeQuery(id+"F59.opExtrude","CAP_FACE",FACE,{"disambiguationData":[OSD([sQuery(id+"F58.wireOp",EDGE,"E30.bottom"),sQuery(id+"F58.wireOp",EDGE,"E30.top"),sQuery(id+"F58.wireOp",EDGE,"E30.left"),sQuery(id+"F58.wireOp",EDGE,"E30.right")])],"isStart":false});
            var sketch = newSketch(context, id + "F62", { "sketchPlane" : qUnion([Q0])});
            skLineSegment(sketch, "E32.bottom", {"start": v(336.55, 501.65) * mm, "end": v(692.15, 501.65) * mm});
            skLineSegment(sketch, "E32.top", {"start": v(336.55, 400.05) * mm, "end": v(692.15, 400.05) * mm});
            skLineSegment(sketch, "E32.left", {"start": v(336.55, 501.65) * mm, "end": v(336.55, 400.05) * mm});
            skLineSegment(sketch, "E32.right", {"start": v(692.15, 501.65) * mm, "end": v(692.15, 400.05) * mm});
            skSolve(sketch);
        }
        {
            var Q0;
            Q0=qSketchRegion(id+"F62",true);
            extrude(context, id + "F63", {"entities" : qUnion([Q0]), "operationType" : NewBodyOperationType.REMOVE, "oppositeDirection" : true, "depth" : 12.7 * mm, "offsetDistance" : 25.4 * mm});
        }
    });
